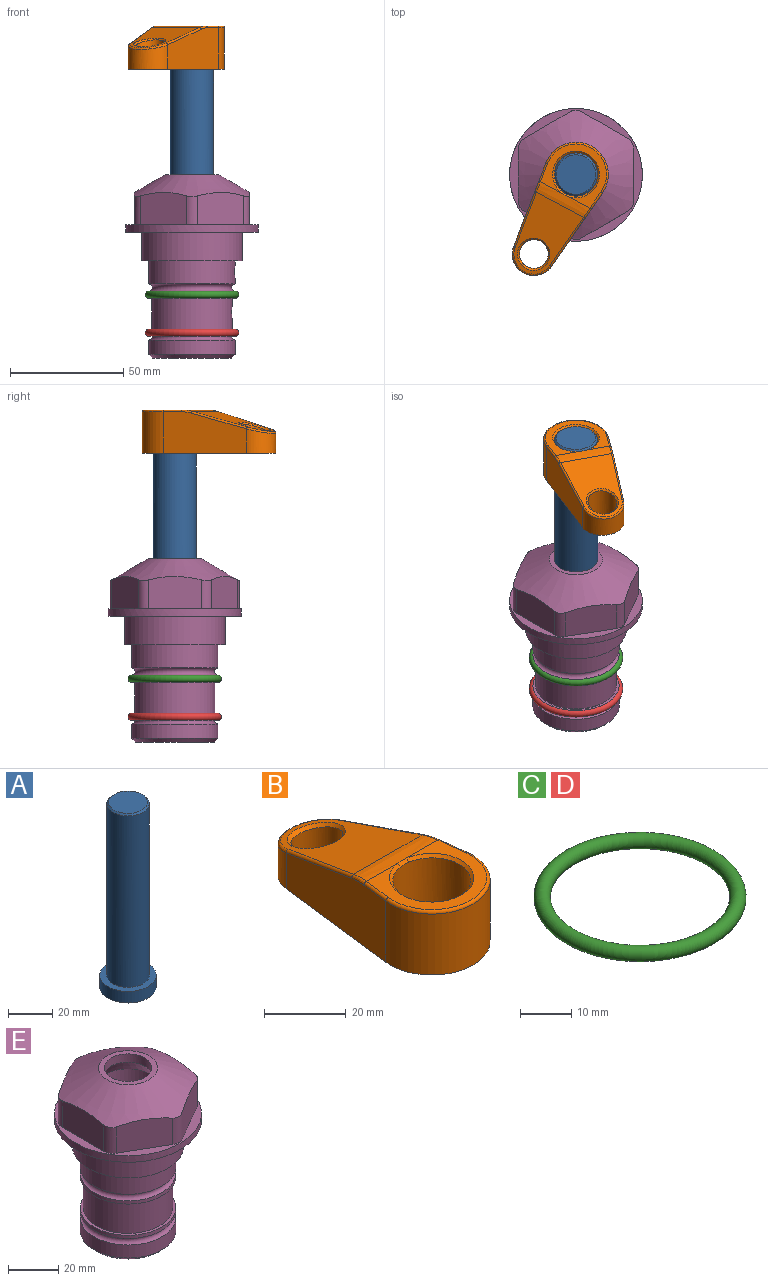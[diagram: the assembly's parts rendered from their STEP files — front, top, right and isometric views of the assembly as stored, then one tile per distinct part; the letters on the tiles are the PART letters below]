
ASSEMBLY  parts=5 mates=5
PART A: 6 faces, bbox 25.4x25.4x101.6 mm
  f0: plane 17.46x17.46mm, normal (0,0,1), area 239.5mm2, adj f5
  f1: plane 25.4x25.4mm, normal (0,0,-1), area 506.7mm2, adj f2
  f2: cylinder r=12.7mm len=25.4mm, axis (0,0,1), area 506.7mm2, adj f1,f3
  f3: plane 25.4x25.4mm, normal (0,0,1), area 221.7mm2, adj f2,f4
  f4: cylinder r=9.53mm len=94.46mm, axis (0,0,1), area 5653mm2, adj f3,f5
  f5: cone r=8.73mm half-angle=45deg, axis (0,0,-1), area 64.4mm2, adj f0,f4
PART B: 31 faces, bbox 31.7x65.5x19.8 mm
  f0: plane 39.12x18.26mm, normal (0.99,0.12,0), area 612.2mm2, adj f1,f4,f7,f11,f13,f15
  f1: cylinder r=9.53mm len=18.91mm, axis (0,0,-1), area 296.1mm2, adj f0,f2,f7,f17
  f2: plane 39.12x18.26mm, normal (-0.99,0.12,0), area 612.2mm2, adj f1,f4,f7,f12,f14,f16
  f3: cylinder r=6.35mm len=12.7mm, axis (0,0,-1), area 362.4mm2, adj f7,f18
  f4: cylinder r=14.29mm len=28.58mm, axis (0,0,-1), area 882.2mm2, adj f0,f2,f7,f10
  f5: cylinder r=9.53mm len=19.05mm, axis (0,0,-1), area 1092.6mm2, adj f7,f19,f20
  f6: plane 26.99x23.69mm, normal (0,0,1), area 216.2mm2, adj f9,f10,f11,f12,f19
  f7: plane 63.5x28.58mm, normal (0,0,-1), area 661.8mm2, adj f0,f1,f2,f3,f4,f5,f22,f23
  f8: plane 33.52x23.6mm, normal (0,0.26,0.97), area 486mm2, adj f9,f15,f16,f17,f18
  f9: cylinder r=19.05mm len=24.72mm, axis (1,0,0), area 120.4mm2, adj f6,f8,f13,f14,f20
  f10: torus R=13.49mm, axis (0,0,1), area 59mm2, adj f4,f6,f11,f12
  f11: cylinder r=0.79mm len=8.67mm, axis (0.12,-0.99,0), area 10.8mm2, adj f0,f6,f10,f13
  f12: cylinder r=0.79mm len=8.67mm, axis (0.12,0.99,0), area 10.8mm2, adj f2,f6,f10,f14
  f13: bspline ~4.95x1.42mm, area 6.1mm2, adj f0,f9,f11,f15
  f14: bspline ~4.95x1.42mm, area 6.1mm2, adj f2,f9,f12,f16
  f15: cylinder r=0.79mm len=25.95mm, axis (0.12,-0.96,0.26), area 32.9mm2, adj f0,f8,f13,f17
  f16: cylinder r=0.79mm len=25.95mm, axis (0.12,0.96,-0.26), area 32.9mm2, adj f2,f8,f14,f17
  f17: bspline ~18.91x8.38mm, area 30mm2, adj f1,f8,f15,f16
  f18: bspline ~14.29x14.29mm, area 48.3mm2, adj f3,f8
  f19: cone r=9.53mm half-angle=45deg, axis (0,0,1), area 66.5mm2, adj f5,f6,f20
  f20: bspline ~3.22x0.96mm, area 3.5mm2, adj f5,f9,f19
  f21: plane 2.75x2.72mm, normal (0,0,-1), area 2.9mm2, adj f23,f25,f28
  f22: plane 23.05x15.88mm, normal (-0.99,-0.12,0), area 323.6mm2, adj f7,f25,f26,f27,f28,f29
  f23: plane 23.05x15.88mm, normal (0.99,-0.12,0), area 323.6mm2, adj f7,f21,f25,f27,f28,f30
  f24: cylinder r=9.53mm len=10.69mm, axis (0,0,-1), area 114.7mm2, adj f7,f27,f29,f30
  f25: cylinder r=12.7mm len=20.59mm, axis (0,0,-1), area 381.1mm2, adj f7,f21,f22,f23,f26,f28
  f26: plane 2.75x2.72mm, normal (0,0,-1), area 2.9mm2, adj f22,f25,f28
  f27: plane 19.72x18.37mm, normal (0,-0.26,-0.97), area 291.8mm2, adj f22,f23,f24,f28,f29,f30
  f28: cylinder r=15.88mm len=19.92mm, axis (1,0,0), area 54.8mm2, adj f21,f22,f23,f25,f26,f27
  f29: cylinder r=1.59mm len=11mm, axis (0,0,-1), area 34.7mm2, adj f7,f22,f24,f27
  f30: cylinder r=1.59mm len=11mm, axis (0,0,-1), area 34.7mm2, adj f7,f23,f24,f27
PART C: 1 faces, bbox 44.7x44.7x3.2 mm
  f0: torus R=19.05mm, axis (0,0,1), area 1193.9mm2
PART D: same geometry as C
PART E: 36 faces, bbox 58.7x58.7x81 mm
  f0: cylinder r=17.78mm len=35.56mm, axis (0,0,1), area 1670.8mm2, adj f23,f24,f31
  f1: cylinder r=19.05mm len=38.1mm, axis (0,0,1), area 1191.9mm2, adj f26,f27,f30
  f2: plane 58.66x58.66mm, normal (0,0,-1), area 1150.6mm2, adj f3,f28
  f3: cylinder r=29.33mm len=58.66mm, axis (0,0,-1), area 585.1mm2, adj f2,f4
  f4: plane 58.66x58.66mm, normal (0,0,1), area 475.9mm2, adj f3,f5,f6,f7,f8,f9,f10,f11
  f5: plane 20.32x14.34mm, normal (-0.5,0.87,0), area 324.4mm2, adj f4,f15,f16,f17
  f6: plane 20.32x14.34mm, normal (0.5,0.87,0), area 324.4mm2, adj f4,f14,f15,f17
  f7: plane 23.48x14.34mm, normal (1,0,0), area 324.4mm2, adj f4,f13,f14,f17
  f8: plane 20.32x14.34mm, normal (0.5,-0.87,0), area 324.4mm2, adj f4,f12,f13,f17
  f9: plane 20.32x14.34mm, normal (-0.5,-0.87,0), area 324.4mm2, adj f4,f11,f12,f17
  f10: plane 23.48x14.34mm, normal (-1,0,0), area 324.4mm2, adj f4,f11,f16,f17
  f11: cylinder r=5.08mm len=12.85mm, axis (0,0,-1), area 67.2mm2, adj f4,f9,f10,f17
  f12: cylinder r=5.08mm len=12.85mm, axis (0,0,-1), area 67.2mm2, adj f4,f8,f9,f17
  f13: cylinder r=5.08mm len=12.85mm, axis (0,0,-1), area 67.2mm2, adj f4,f7,f8,f17
  f14: cylinder r=5.08mm len=12.85mm, axis (0,0,-1), area 67.2mm2, adj f4,f6,f7,f17
  f15: cylinder r=5.08mm len=12.85mm, axis (0,0,-1), area 67.2mm2, adj f4,f5,f6,f17
  f16: cylinder r=5.08mm len=12.85mm, axis (0,0,-1), area 67.2mm2, adj f4,f5,f10,f17
  f17: cone r=11.73mm half-angle=60deg, axis (0,0,-1), area 2071.8mm2, adj f5,f6,f7,f8,f9,f10,f11,f12
  f18: plane 23.46x23.46mm, normal (0,0,1), area 147.4mm2, adj f17,f35
  f19: plane 34.93x34.93mm, normal (0,0,-1), area 958mm2, adj f29
  f20: cylinder r=19.05mm len=38.1mm, axis (0,0,1), area 760.1mm2, adj f21,f29
  f21: torus R=19.05mm, axis (0,0,1), area 565.3mm2, adj f20,f22
  f22: cylinder r=19.05mm len=38.1mm, axis (0,0,1), area 190mm2, adj f21,f23
  f23: plane 38.1x38.1mm, normal (0,0,1), area 146.9mm2, adj f0,f22
  f24: plane 38.1x38.1mm, normal (0,0,-1), area 146.9mm2, adj f0,f25
  f25: cylinder r=19.05mm len=38.1mm, axis (0,0,1), area 190mm2, adj f24,f26
  f26: torus R=19.05mm, axis (0,0,1), area 565.3mm2, adj f1,f25
  f27: plane 44.45x44.45mm, normal (0,0,-1), area 411.7mm2, adj f1,f28
  f28: cylinder r=22.23mm len=44.45mm, axis (0,0,1), area 1773.5mm2, adj f2,f27
  f29: cone r=19.05mm half-angle=45deg, axis (0,0,1), area 257.5mm2, adj f19,f20
  f30: cylinder r=3.17mm len=6.75mm, axis (-1,0,0), area 128mm2, adj f1,f33
  f31: cylinder r=3.17mm len=6.35mm, axis (-1,0,0), area 102.5mm2, adj f0,f33
  f32: plane 25.4x25.4mm, normal (0,0,1), area 506.7mm2, adj f33
  f33: cylinder r=12.7mm len=66.42mm, axis (0,0,-1), area 5236.2mm2, adj f30,f31,f32,f34
  f34: cone r=9.53mm half-angle=30deg, axis (0,0,-1), area 443.4mm2, adj f33,f35
  f35: cylinder r=9.53mm len=19.05mm, axis (0,0,-1), area 240.9mm2, adj f18,f34
PLACE A rot(axis=(0,0,1),152deg) t=(0,0,27.55)mm
PLACE B rot(axis=(0,0,1),152deg) t=(0,0,27.55)mm
PLACE C t=(0,0,-3.18)mm
PLACE D t=(0,0,-20)mm
PLACE E at identity fixed
MATE cylindrical A.f2 <-> E.f0  axis (0,0,-1) through (0,0,-10.55)mm
MATE cylindrical A.f2 <-> E.f0  axis (0,0,-1) through (0,0,-10.55)mm
MATE fastened C.f0 <-> E.f0  axis (0,0,1) through (0,0,-27.69)mm
MATE fastened A.f2 <-> B.f4  axis (0,0,1) through (0,0,91.05)mm
MATE fastened D.f0 <-> E.f0  axis (0,0,1) through (0,0,-44.51)mm
